# Revit family: Haworth_Janus_Slant_Table_Occasional_Round
name_source: partatom
category: Furniture
revit_build: Autodesk Revit 2018 (Build: 20170223_1515(x64)
units: mm (PartAtom-declared; Revit-internal decimal feet)

## family parameters
Always vertical = Yes
Cut with Voids When Loaded = No
OmniClass Number = 23.40.70.14.64.21
OmniClass Title = Systems Furniture
Room Calculation Point = No
Shared = No
Work Plane-Based = No

## types (1)
- HCJC-SL-TON20-G
    Actual Depth = 20"
    Actual Height = 19 3/4"
    Actual Width = 20"
    Assembly Code = E2020200
    Description = Haworth Janus Slant Round Occasional Table
    Manufacturer = Haworth
    Model = HCJC-SL-TON20-G
    Radius = 10"
    Revision Number = 2
    Size = Verify Final Dim. w/ Haworth
    Standard Depths = 20 in.
    Standard Height = 19.75 in.
    Table Thickness = 19 3/8"
    Top Finish = Haworth _ Glass _ Frosted
    URL = http://www.haworth.com
    URL - Product = https://www.haworth.com
    Warranty = https://www.haworth.com

## geometry (parser evidence)
native form markers: Sweep x3
no freeform markers — native parametric forms only
